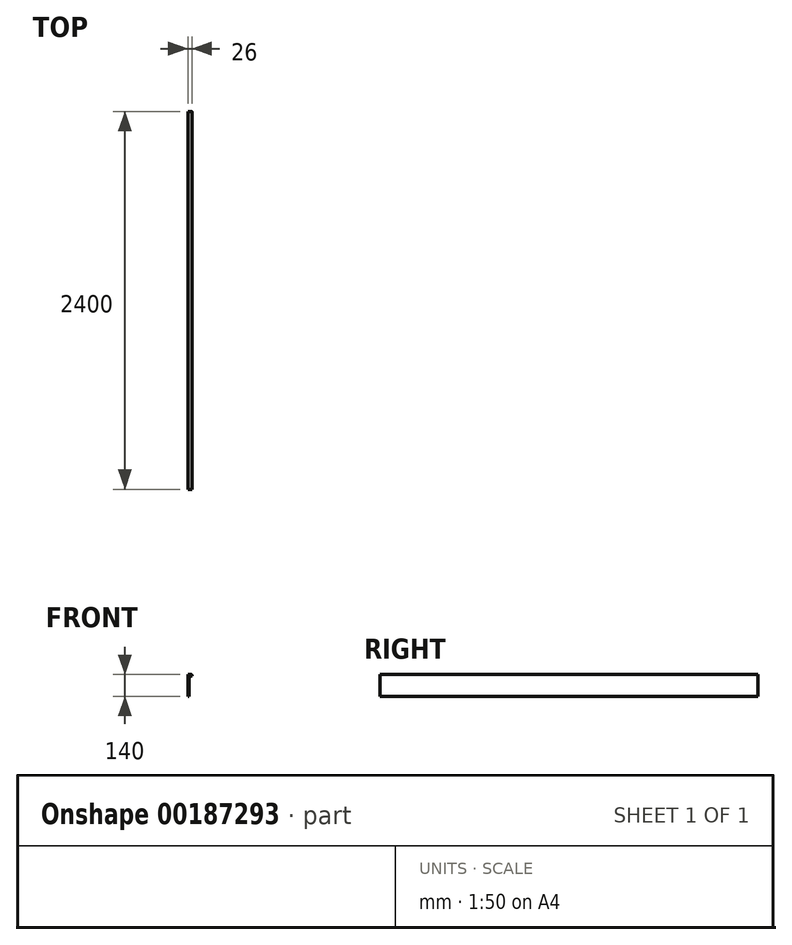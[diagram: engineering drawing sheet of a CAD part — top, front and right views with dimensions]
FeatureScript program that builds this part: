
annotation { "Feature Type Name" : "Feature", "Feature Type Description" : "" }
export const myFeature = defineFeature(function(context is Context, id is Id, definition is map)
    precondition{}
    {
        {
            var Q0;
            Q0=qCreatedBy(makeId("Front.planeOp"),FACE);
            var sketch = newSketch(context, id + "F0", { "sketchPlane" : qUnion([Q0])});
            skLineSegment(sketch, "E0.bottom", {"start": v(0, 0) * mm, "end": v(7, 0) * mm});
            skLineSegment(sketch, "E0.left", {"start": v(0, 0) * mm, "end": v(0, 140) * mm});
            skLineSegment(sketch, "E0.right", {"start": v(7, 0) * mm, "end": v(7, 116.68) * mm});
            skArc(sketch, "E1", {"start": v(23, 128.8) * mm, "mid": v(25.8, 135.55) * mm, "end": v(20, 140) * mm});
            skLineSegment(sketch, "E2", {"start": v(23, 128.8) * mm, "end": v(9.5, 121) * mm});
            skLineSegment(sketch, "E3", {"start": v(0, 140) * mm, "end": v(20, 140) * mm});
            skPoint(sketch, "E4.visualSharp", {"position": v(7, 103.82) * mm});
            skArc(sketch, "E4.filletArc", {"start": v(9.5, 121) * mm, "mid": v(7.67, 119.18) * mm, "end": v(7, 116.68) * mm});
            skSolve(sketch);
        }
        {
            var Q0;
            Q0=qSketchRegion(id+"F0",true);
            extrude(context, id + "F1", {"entities" : qUnion([Q0]), "depth" : 2400 * mm});
        }
    });
